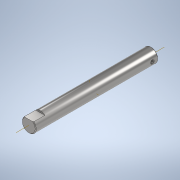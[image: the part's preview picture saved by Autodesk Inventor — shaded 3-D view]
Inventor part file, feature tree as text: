
AUTODESK INVENTOR PART (.ipt)
format: ipt  version: 2021.1 (Build 251245000, 245)  size: 129,024 bytes
history: native  units: in
note: dims shown in document units (in); Inventor stores cm internally (conversion verified against a paired STEP export)
features: extrude x2, sketch x2, projected_geometry x2, chamfer x1
ambient origin geometry x8: Origin, YZ Plane, XZ Plane, XY Plane, X Axis, Y Axis, Z Axis, Center Point
bodies: Solid1 (feature_tree)
feature tree (7):
  extrude  "Extrusion1"  Depth=10.6in TaperAngle=0.0deg
  extrude  "Extrusion2"  Depth=0.5in
  chamfer  "Chamfer1"  Distance=0.32in
  sketch  "Sketch1"  dims[d0=1.2in d1=10.6in d2=0.0in]
  sketch  "Sketch2"  dims[d3=0.3in d4=0.5in d5=0.32in d6=1.0in d7=0.45in d8=0.0in d9=0.0in d10=0.05in d11=0.125in d12=45.0deg]
  projected_geometry  "Projected Loop1"
  projected_geometry  "Project Cut Edges1"
